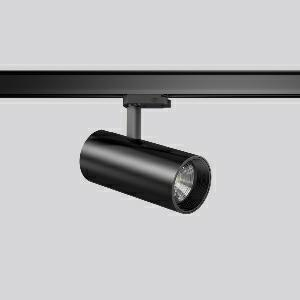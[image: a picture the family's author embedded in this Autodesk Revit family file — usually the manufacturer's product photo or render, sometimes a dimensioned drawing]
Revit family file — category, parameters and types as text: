
# Revit family: deecos_s_mini_742206_003_c032
name_source: partatom
category: Lighting Fixtures
units: mm (PartAtom-declared; Revit-internal decimal feet)

## family parameters
Cut with Voids When Loaded = No
Host = Face
Light Source = No
Part Type = Normal
Room Calculation Point = No
Round Connector Dimension = Use Diameter
Shared = No

## types (1)
- DEECOS S mini (1 x LED Modul 930, 3150 lm, 3000)
    Apparent Load = 29 VA
    Approval mark = CE
    CIE Flux Codes = 99 100 100 100 100
    Color Rendering = 90
    Color Temperature = 3000
    Default Elevation = 1800 mm
    Description = Series: DEECOS S mini
LED surface-mounted projector in modern design with no visible cooling ribs. Housing: die-cast aluminium, powder-coated. Rotation range: 356°. Swivel range: 90°. Black plastic ring and recessed LED to prevent glare from the side. Optical assembly with lens made of plastic (polycarbonate) for the best homogeneous light distribution - can be changed without tools. Best colour rendering index Ra>90. With multi adaptor for 3-circuit tracks 230 V. Suitable for Track on ceiling, Wall track. High quality converter without flickering and stroboscopic effect. The following accessories can be mounted without use of tools: interchangeable lenses, decorative glasses, honeycomb louvre, clear and frosted diffusers, white interchangeable plastic ring. 
Colour: deep black, matt (RAL 9005)
Diameter: 87 mm
Height: 214 mm
Lamp: LED
Socket: without socket
Colour temperature: 3000K
Colour rendering index (CRI): 92
System power: 29 W
Rated luminous flux: 3150 lm
Luminous efficiency: 109 lm/W
Control gear: Regulated power supply
Protection class: I
Type of protection: IP 20
    Height = 214 mm
    Lamp = 1 x LED Modul 930
    Lamp Light Flux = 3150 lm
    Lamp count = 1
    Length = 87 mm
    Lifetime = 50000 h
    Luminous efficacy = 109 lm/W
    Manufacturer = RZB
    ModVariant = No
    Model = 742206.003
    Mounting Place = Ceiling
    Mounting Type = Rail mounted
    Number of Poles = 1
    OnlyDefault = Yes
    Power Factor = 1
    Product Name = DEECOS S mini
    Product group = Track mounted projectors
    ProductGroupID = 301
    Protection Class = Protection class I
    Protection Degree = IP 20
    RLX_Detail_Level = 1
    RLX_Emergency_Light_Flux = 0 lm
    RLX_Emergency_Type = 0
    RLX_Emergency_Type_DB = No
    RlxData = <blob elided: 39073 chars, md5=99af3f1f>
    Socket = socket
    Standby Power = 0 W
    System Light Flux = 3150 lm
    System Power = 29 W
    Type Comments = Product without accessories
    Type Image = 741930.003.jpg
    URL = http://relux.com
    VarID = ---
    Voltage = 230 V
    Voltage Range = 220-240 V
    Weight = 0.00 kg
    Width = 0 mm  [stored 0 ft]

note: [stored X ft] marks values corroborated as IEEE doubles in the binary element streams (Revit-internal decimal feet)

## geometry (parser evidence)
native form markers: Blend x4, Sweep x10
no freeform markers — native parametric forms only
